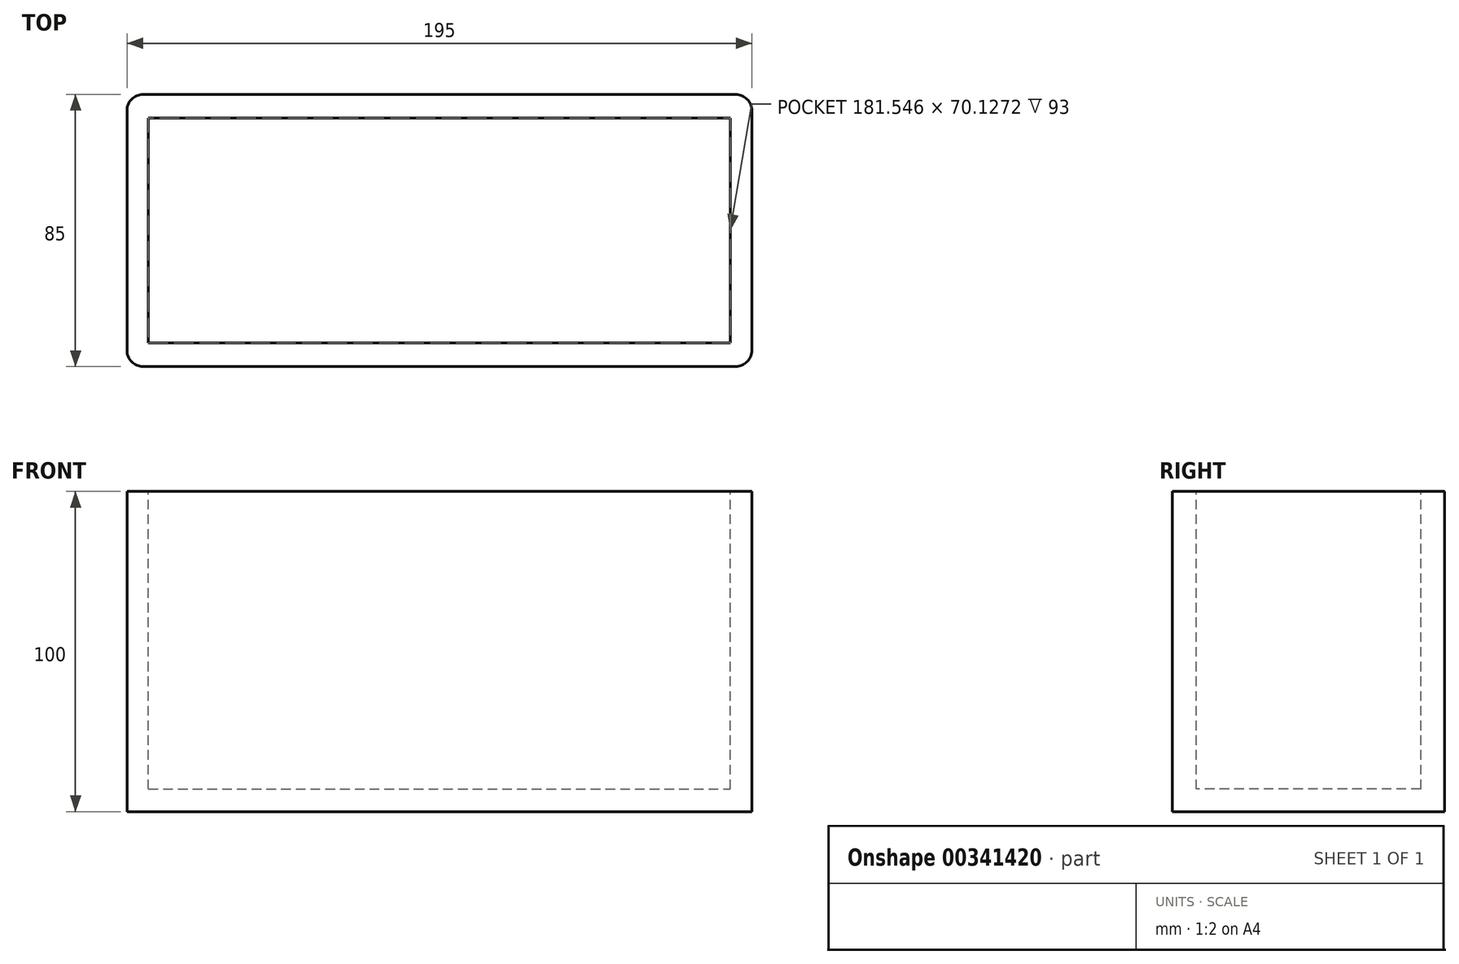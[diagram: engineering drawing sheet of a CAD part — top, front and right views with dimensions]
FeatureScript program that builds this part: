
annotation { "Feature Type Name" : "Feature", "Feature Type Description" : "" }
export const myFeature = defineFeature(function(context is Context, id is Id, definition is map)
    precondition{}
    {
        {
            var Q0;
            Q0=qCreatedBy(makeId("Top.planeOp"),FACE);
            var sketch = newSketch(context, id + "F0", { "sketchPlane" : qUnion([Q0])});
            skLineSegment(sketch, "E0.bottom", {"start": v(-97.5, 42.5) * mm, "end": v(97.5, 42.5) * mm});
            skLineSegment(sketch, "E0.top", {"start": v(-97.5, -42.5) * mm, "end": v(97.5, -42.5) * mm});
            skLineSegment(sketch, "E0.left", {"start": v(-97.5, 42.5) * mm, "end": v(-97.5, -42.5) * mm});
            skLineSegment(sketch, "E0.right", {"start": v(97.5, 42.5) * mm, "end": v(97.5, -42.5) * mm});
            skPoint(sketch, "E0.middle", {"position": v(0, 0) * mm});
            skSolve(sketch);
        }
        {
            var Q0;
            Q0 = qSketchRegion(id + "F0", true);
            var Q1;
            Q1=makeQuery(id+"F0.imprint","IMPRINT",FACE,{"disambiguationData":[TD([[makeQuery(id+"F0.imprint","IMPRINT",EDGE,{"derivedFrom":sQuery(id+"F0.wireOp",EDGE,"E0.bottom")}),-1.0]])]});
            extrude(context, id + "F1", {"entities" : qUnion([Q0, Q1]), "depth" : 100 * mm});
        }
        {
            var Q0;
            Q0=makeQuery(id+"F1.opExtrude","CAP_FACE",FACE,{"disambiguationData":[OSD([sQuery(id+"F0.wireOp",EDGE,"E0.bottom"),sQuery(id+"F0.wireOp",EDGE,"E0.top"),sQuery(id+"F0.wireOp",EDGE,"E0.left"),sQuery(id+"F0.wireOp",EDGE,"E0.right")])],"isStart":false});
            var sketch = newSketch(context, id + "F2", { "sketchPlane" : qUnion([Q0])});
            skPoint(sketch, "E1.middle", {"position": v(1.31, 0) * mm});
            skLineSegment(sketch, "E2.bottom", {"start": v(-90.77, 35.06) * mm, "end": v(90.77, 35.06) * mm});
            skLineSegment(sketch, "E2.top", {"start": v(-90.77, -35.06) * mm, "end": v(90.77, -35.06) * mm});
            skLineSegment(sketch, "E2.left", {"start": v(-90.77, 35.06) * mm, "end": v(-90.77, -35.06) * mm});
            skLineSegment(sketch, "E2.right", {"start": v(90.77, 35.06) * mm, "end": v(90.77, -35.06) * mm});
            skPoint(sketch, "E2.middle", {"position": v(0, 0) * mm});
            skSolve(sketch);
        }
        {
            var Q0;
            Q0 = qSketchRegion(id + "F2", true);
            var Q1;
            Q1=makeQuery(id+"F2.imprint","IMPRINT",FACE,{"disambiguationData":[TD([[makeQuery(id+"F2.imprint","IMPRINT",EDGE,{"derivedFrom":sQuery(id+"F2.wireOp",EDGE,"E2.bottom")}),-1.0]])]});
            extrude(context, id + "F3", {"entities" : qUnion([Q0, Q1]), "operationType" : NewBodyOperationType.REMOVE, "oppositeDirection" : true, "depth" : 93 * mm});
        }
        {
            var Q0;
            Q0=makeQuery(id+"F1.opExtrude","SWEPT_EDGE",EDGE,{"disambiguationData":[OSD([sQuery(id+"F0.wireOp",EDGE,"E0.top"),sQuery(id+"F0.wireOp",EDGE,"E0.right")])]});
            var Q1;
            Q1=makeQuery(id+"F1.opExtrude","SWEPT_EDGE",EDGE,{"disambiguationData":[OSD([sQuery(id+"F0.wireOp",EDGE,"E0.bottom"),sQuery(id+"F0.wireOp",EDGE,"E0.right")])]});
            var Q2;
            Q2=makeQuery(id+"F1.opExtrude","SWEPT_EDGE",EDGE,{"disambiguationData":[OSD([sQuery(id+"F0.wireOp",EDGE,"E0.top"),sQuery(id+"F0.wireOp",EDGE,"E0.left")])]});
            var Q3;
            Q3=makeQuery(id+"F1.opExtrude","SWEPT_EDGE",EDGE,{"disambiguationData":[OSD([sQuery(id+"F0.wireOp",EDGE,"E0.bottom"),sQuery(id+"F0.wireOp",EDGE,"E0.left")])]});
            fillet(context, id + "F4", {"entities" : qUnion([Q0, Q1, Q2, Q3]), "radius" : 5.08 * mm, "tangentPropagation" : true, "allowEdgeOverflow" : false});
        }
    });
